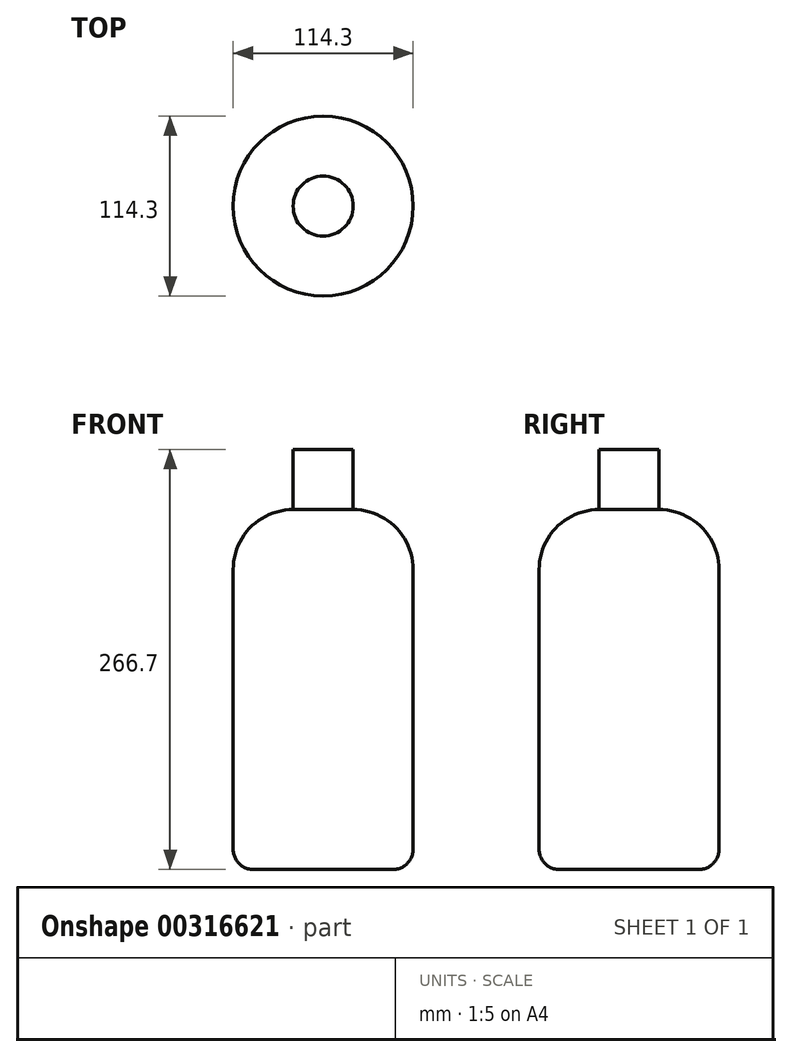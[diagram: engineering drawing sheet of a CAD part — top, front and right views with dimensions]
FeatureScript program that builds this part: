
annotation { "Feature Type Name" : "Feature", "Feature Type Description" : "" }
export const myFeature = defineFeature(function(context is Context, id is Id, definition is map)
    precondition{}
    {
        {
            var Q0;
            Q0=qCreatedBy(makeId("Front.planeOp"),FACE);
            var sketch = newSketch(context, id + "F0", { "sketchPlane" : qUnion([Q0])});
            skLineSegment(sketch, "E0.bottom", {"start": v(17.37, 199.65) * mm, "end": v(55.47, 199.65) * mm});
            skLineSegment(sketch, "E0.top", {"start": v(-8.03, -28.95) * mm, "end": v(80.87, -28.95) * mm});
            skLineSegment(sketch, "E0.left", {"start": v(-20.73, 161.55) * mm, "end": v(-20.73, -16.25) * mm});
            skLineSegment(sketch, "E0.right", {"start": v(93.57, 161.55) * mm, "end": v(93.57, -16.25) * mm});
            skPoint(sketch, "E1.visualSharp", {"position": v(-20.73, 199.65) * mm});
            skArc(sketch, "E1.filletArc", {"start": v(17.37, 199.65) * mm, "mid": v(-9.57, 188.49) * mm, "end": v(-20.73, 161.55) * mm});
            skPoint(sketch, "E2.visualSharp", {"position": v(93.57, 199.65) * mm});
            skArc(sketch, "E2.filletArc", {"start": v(93.57, 161.55) * mm, "mid": v(82.4, 188.49) * mm, "end": v(55.47, 199.65) * mm});
            skPoint(sketch, "E3.visualSharp", {"position": v(-20.73, -28.95) * mm});
            skArc(sketch, "E3.filletArc", {"start": v(-20.73, -16.25) * mm, "mid": v(-17.01, -25.23) * mm, "end": v(-8.03, -28.95) * mm});
            skPoint(sketch, "E4.visualSharp", {"position": v(93.57, -28.95) * mm});
            skArc(sketch, "E4.filletArc", {"start": v(80.87, -28.95) * mm, "mid": v(89.85, -25.23) * mm, "end": v(93.57, -16.25) * mm});
            skLineSegment(sketch, "E5.top", {"start": v(17.37, 237.75) * mm, "end": v(55.47, 237.75) * mm});
            skLineSegment(sketch, "E5.left", {"start": v(17.37, 199.65) * mm, "end": v(17.37, 237.75) * mm});
            skLineSegment(sketch, "E5.right", {"start": v(55.47, 199.65) * mm, "end": v(55.47, 237.75) * mm});
            skLineSegment(sketch, "E6", {"start": v(36.42, 259.72) * mm, "end": v(36.42, -52.57) * mm});
            skSolve(sketch);
        }
        {
            var Q0;
            Q0=makeQuery(id+"F0.imprint","IMPRINT",FACE,{"disambiguationData":[TD([[makeQuery(id+"F0.imprint","IMPRINT",EDGE,{"derivedFrom":sQuery(id+"F0.wireOp",EDGE,"E0.right")}),-1.0]])]});
            var Q1;
            {var subQ0=sQuery(id+"F0.wireOp",EDGE,"E5.right");Q1=makeQuery(id+"F0.imprint","IMPRINT",FACE,{"disambiguationData":[TD([[makeQuery(id+"F0.imprint","IMPRINT",EDGE,{"derivedFrom":subQ0}),1.0]])]});}
            var Q2;
            Q2=sQuery(id+"F0.wireOp",EDGE,"E6");
            revolve(context, id + "F1", {"entities" : qUnion([Q0, Q1]), "axis" : qUnion([Q2]), "revolveType" : RevolveType.FULL});
        }
    });
